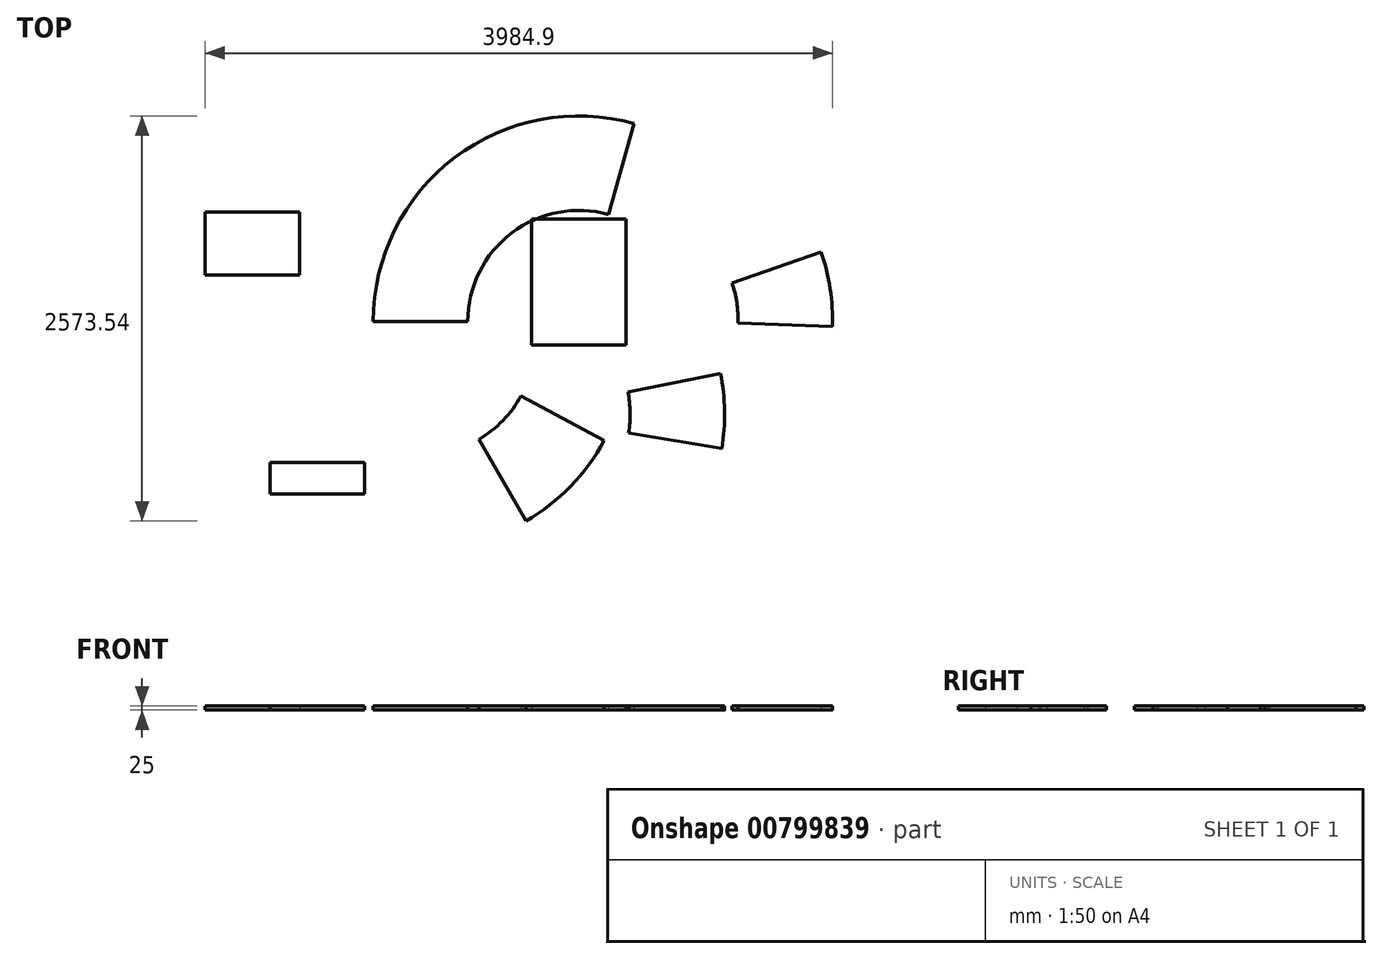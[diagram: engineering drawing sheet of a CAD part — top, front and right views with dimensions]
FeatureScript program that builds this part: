
annotation { "Feature Type Name" : "Feature", "Feature Type Description" : "" }
export const myFeature = defineFeature(function(context is Context, id is Id, definition is map)
    precondition{}
    {
        {
            var Q0;
            Q0=qCreatedBy(makeId("Top.planeOp"),FACE);
            var sketch = newSketch(context, id + "F0", { "sketchPlane" : qUnion([Q0])});
            skArc(sketch, "E0", {"start": v(351.23, 1256.85) * mm, "mid": v(-788.88, 1039.56) * mm, "end": v(-1305, 0) * mm});
            skArc(sketch, "E1", {"start": v(189.75, 678.99) * mm, "mid": v(-426.18, 561.6) * mm, "end": v(-705, 0) * mm});
            skPoint(sketch, "E2", {"position": v(-1305, 0) * mm});
            skLineSegment(sketch, "E3", {"start": v(-705, 0) * mm, "end": v(-1305, 0) * mm});
            skLineSegment(sketch, "E4", {"start": v(189.75, 678.99) * mm, "end": v(351.23, 1256.85) * mm});
            skSolve(sketch);
        }
        {
            var Q0;
            Q0=qSketchRegion(id+"F0",true);
            extrude(context, id + "F1", {"entities" : qUnion([Q0]), "depth" : 25 * mm, "offsetDistance" : 25 * mm});
        }
        {
            var Q0;
            Q0=qCreatedBy(makeId("Top.planeOp"),FACE);
            var sketch = newSketch(context, id + "F2", { "sketchPlane" : qUnion([Q0])});
            skLineSegment(sketch, "E5.bottom", {"start": v(-1773.73, 295.8) * mm, "end": v(-2373.73, 295.8) * mm});
            skLineSegment(sketch, "E5.top", {"start": v(-1773.73, 695.8) * mm, "end": v(-2373.73, 695.8) * mm});
            skLineSegment(sketch, "E5.left", {"start": v(-2373.73, 695.8) * mm, "end": v(-2373.73, 295.8) * mm});
            skLineSegment(sketch, "E5.right", {"start": v(-1773.73, 695.8) * mm, "end": v(-1773.73, 295.8) * mm});
            skSolve(sketch);
        }
        {
            var Q0;
            Q0=qSketchRegion(id+"F2",true);
            extrude(context, id + "F3", {"entities" : qUnion([Q0]), "depth" : 25 * mm, "offsetDistance" : 25 * mm});
        }
        {
            var Q0;
            Q0=qCreatedBy(makeId("Top.planeOp"),FACE);
            var sketch = newSketch(context, id + "F4", { "sketchPlane" : qUnion([Q0])});
            skArc(sketch, "E6", {"start": v(1610.3, -32.85) * mm, "mid": v(1596.9, 206.98) * mm, "end": v(1539.77, 440.28) * mm});
            skArc(sketch, "E7", {"start": v(1010.7, -11.06) * mm, "mid": v(1003.46, 118.5) * mm, "end": v(972.6, 244.54) * mm});
            skPoint(sketch, "E8", {"position": v(1539.77, 440.28) * mm});
            skLineSegment(sketch, "E9", {"start": v(972.6, 244.54) * mm, "end": v(1539.77, 440.28) * mm});
            skLineSegment(sketch, "E10", {"start": v(1010.7, -11.06) * mm, "end": v(1610.3, -32.85) * mm});
            skSolve(sketch);
        }
        {
            var Q0;
            Q0=makeQuery(id+"F4.imprint","IMPRINT",FACE,{"disambiguationData":[TD([[makeQuery(id+"F4.imprint","IMPRINT",EDGE,{"derivedFrom":sQuery(id+"F4.wireOp",EDGE,"E6")}),1.0]])]});
            extrude(context, id + "F5", {"entities" : qUnion([Q0]), "depth" : 25 * mm, "offsetDistance" : 25 * mm});
        }
        {
            var Q0;
            Q0=qCreatedBy(makeId("Top.planeOp"),FACE);
            var sketch = newSketch(context, id + "F6", { "sketchPlane" : qUnion([Q0])});
            skLineSegment(sketch, "E11.bottom", {"start": v(300, -150) * mm, "end": v(-300, -150) * mm});
            skLineSegment(sketch, "E11.top", {"start": v(300, 650) * mm, "end": v(-300, 650) * mm});
            skLineSegment(sketch, "E11.left", {"start": v(-300, 650) * mm, "end": v(-300, -150) * mm});
            skLineSegment(sketch, "E11.right", {"start": v(300, 650) * mm, "end": v(300, -150) * mm});
            skSolve(sketch);
        }
        {
            var Q0;
            Q0=qSketchRegion(id+"F6",true);
            extrude(context, id + "F7", {"entities" : qUnion([Q0]), "depth" : 25 * mm, "offsetDistance" : 25 * mm});
        }
        {
            var Q0;
            Q0=qCreatedBy(makeId("Top.planeOp"),FACE);
            var sketch = newSketch(context, id + "F8", { "sketchPlane" : qUnion([Q0])});
            skLineSegment(sketch, "E12.bottom", {"start": v(-1359.77, -1096.74) * mm, "end": v(-1959.77, -1096.74) * mm});
            skLineSegment(sketch, "E12.top", {"start": v(-1359.77, -896.74) * mm, "end": v(-1959.77, -896.74) * mm});
            skLineSegment(sketch, "E12.left", {"start": v(-1959.77, -896.74) * mm, "end": v(-1959.77, -1096.74) * mm});
            skLineSegment(sketch, "E12.right", {"start": v(-1359.77, -896.74) * mm, "end": v(-1359.77, -1096.74) * mm});
            skSolve(sketch);
        }
        {
            var Q0;
            Q0=makeQuery(id+"F8.imprint","IMPRINT",FACE,{"disambiguationData":[TD([[makeQuery(id+"F8.imprint","IMPRINT",EDGE,{"derivedFrom":sQuery(id+"F8.wireOp",EDGE,"E12.bottom")}),-1.0]])]});
            extrude(context, id + "F9", {"entities" : qUnion([Q0]), "depth" : 25 * mm, "offsetDistance" : 25 * mm});
        }
        {
            var Q0;
            Q0=qCreatedBy(makeId("Top.planeOp"),FACE);
            var sketch = newSketch(context, id + "F10", { "sketchPlane" : qUnion([Q0])});
            skArc(sketch, "E13", {"start": v(908.09, -808.07) * mm, "mid": v(926.21, -568.55) * mm, "end": v(900.13, -329.77) * mm});
            skArc(sketch, "E14", {"start": v(316.5, -707.92) * mm, "mid": v(326.3, -578.53) * mm, "end": v(312.2, -449.53) * mm});
            skPoint(sketch, "E15", {"position": v(900.13, -329.77) * mm});
            skLineSegment(sketch, "E16", {"start": v(312.2, -449.53) * mm, "end": v(900.13, -329.77) * mm});
            skLineSegment(sketch, "E17", {"start": v(316.5, -707.92) * mm, "end": v(908.09, -808.07) * mm});
            skSolve(sketch);
        }
        {
            var Q0;
            Q0=makeQuery(id+"F10.imprint","IMPRINT",FACE,{"disambiguationData":[TD([[makeQuery(id+"F10.imprint","IMPRINT",EDGE,{"derivedFrom":sQuery(id+"F10.wireOp",EDGE,"E13")}),1.0]])]});
            extrude(context, id + "F11", {"entities" : qUnion([Q0]), "depth" : 25 * mm, "offsetDistance" : 25 * mm});
        }
        {
            var Q0;
            Q0=qCreatedBy(makeId("Top.planeOp"),FACE);
            var sketch = newSketch(context, id + "F12", { "sketchPlane" : qUnion([Q0])});
            skArc(sketch, "E18", {"start": v(-334.66, -1268.54) * mm, "mid": v(-51.04, -1047.36) * mm, "end": v(161.44, -757.16) * mm});
            skArc(sketch, "E19", {"start": v(-634.9, -749.06) * mm, "mid": v(-481.69, -629.58) * mm, "end": v(-366.9, -472.8) * mm});
            skPoint(sketch, "E20", {"position": v(161.44, -757.16) * mm});
            skLineSegment(sketch, "E21", {"start": v(-366.9, -472.8) * mm, "end": v(161.44, -757.16) * mm});
            skLineSegment(sketch, "E22", {"start": v(-634.9, -749.06) * mm, "end": v(-334.66, -1268.54) * mm});
            skSolve(sketch);
        }
        {
            var Q0;
            Q0=qSketchRegion(id+"F12",true);
            extrude(context, id + "F13", {"entities" : qUnion([Q0]), "depth" : 25 * mm, "offsetDistance" : 25 * mm});
        }
    });
